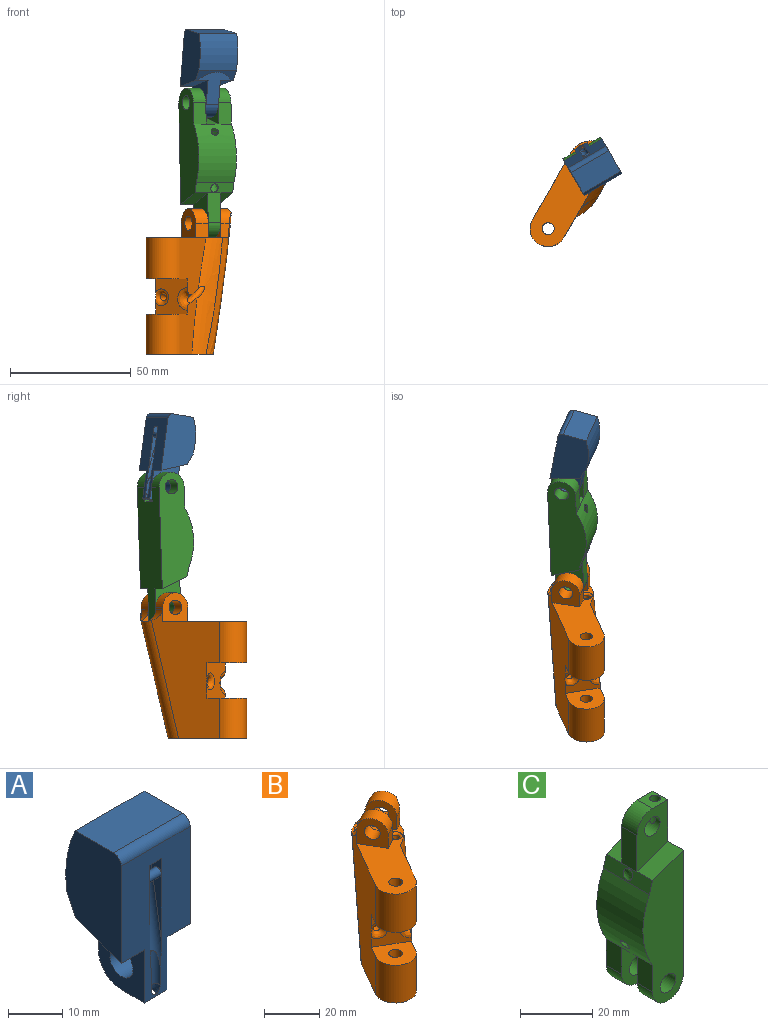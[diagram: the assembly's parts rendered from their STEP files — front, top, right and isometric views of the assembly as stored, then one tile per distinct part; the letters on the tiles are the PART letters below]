
ASSEMBLY  parts=3 mates=5
PART A: 30 faces, bbox 18x15.6x37.3 mm
  f0: cylinder r=5mm len=2.03mm, axis (-1,0,0), area 0.1mm2, adj f25,f29
  f1: plane 23.37x16mm, normal (0,1,0), area 258.7mm2, adj f4,f9,f10,f12,f13,f16,f17,f18
  f2: plane 18x4.63mm, normal (0,0.91,-0.42), area 48.6mm2, adj f7,f8,f12,f13,f15,f16
  f3: plane 6x5.9mm, normal (0,0,-1), area 28.7mm2, adj f4,f5,f9,f10,f28
  f4: cylinder r=6mm len=6mm, axis (-1,0,0), area 55.6mm2, adj f1,f3,f9,f10
  f5: plane 34x18mm, normal (0,-1,0), area 382.9mm2, adj f3,f7,f8,f9,f10,f12,f13,f14
  f6: plane 18x10mm, normal (0,0,1), area 180mm2, adj f7,f8,f14,f15
  f7: plane 24x14.5mm, normal (1,0,0), area 294.1mm2, adj f2,f5,f6,f12,f14,f15
  f8: plane 24x14.5mm, normal (-1,0,0), area 294.1mm2, adj f2,f5,f6,f13,f14,f15
  f9: plane 16.37x12mm, normal (1,0,0), area 134.2mm2, adj f1,f3,f4,f5,f11,f12
  f10: plane 16.37x12mm, normal (-1,0,0), area 134.2mm2, adj f1,f3,f4,f5,f11,f13
  f11: cylinder r=3mm len=6mm, axis (-1,0,0), area 111.2mm2, adj f9,f10
  f12: plane 12x6.05mm, normal (0,0.34,-0.94), area 77.3mm2, adj f1,f2,f5,f7,f9
  f13: plane 12x6.05mm, normal (0,0.34,-0.94), area 77.3mm2, adj f1,f2,f5,f8,f10
  f14: cylinder r=2mm len=18mm, axis (-1,0,0), area 56.5mm2, adj f5,f6,f7,f8
  f15: cylinder r=24.92mm len=18mm, axis (1,0,0), area 277.2mm2, adj f2,f6,f7,f8
  f16: cylinder r=19.67mm len=16mm, axis (0,0,-1), area 163.7mm2, adj f1,f2,f17,f18,f19,f20,f21
  f17: plane 16x1.7mm, normal (0,0,-1), area 18.3mm2, adj f1,f16
  f18: plane 3x1.7mm, normal (0,0,1), area 5mm2, adj f1,f16,f20,f21
  f19: plane 3x1.7mm, normal (0,0,-1), area 5mm2, adj f1,f16,f20,f21
  f20: plane 3.5x1.64mm, normal (-1,0,0), area 5.7mm2, adj f1,f16,f18,f19
  f21: plane 3.5x1.64mm, normal (1,0,0), area 5.7mm2, adj f1,f16,f18,f19
  f22: plane 4.48x3mm, normal (0,-0.16,-0.99), area 12.7mm2, adj f5,f23,f24,f25
  f23: plane 18.5x3mm, normal (-1,0,0), area 24.6mm2, adj f5,f22,f25,f26
  f24: plane 18.5x3mm, normal (1,0,0), area 24.6mm2, adj f5,f22,f25,f26
  f25: cylinder r=1.5mm len=23.99mm, axis (0,0.16,0.99), area 99mm2, adj f0,f5,f22,f23,f24,f27,f29
  f26: cylinder r=1mm len=3mm, axis (1,0,0), area 18.8mm2, adj f23,f24
  f27: cylinder r=5mm len=2.03mm, axis (-1,0,0), area 0.1mm2, adj f25,f29
  f28: bspline ~5.45x3.42mm, area 16.3mm2, adj f3,f5,f29
  f29: cylinder r=1.14mm len=7.64mm, axis (0,0,-1), area 24.2mm2, adj f0,f5,f25,f27,f28
PART B: 44 faces, bbox 55.1x59.7x84.5 mm
  f0: plane 23.52x12.49mm, normal (0.87,-0.5,0), area 223.6mm2, adj f5,f13,f24,f26,f28,f37,f38
  f1: plane 23.82x19mm, normal (0.87,-0.5,0), area 376.7mm2, adj f4,f14,f24,f25,f28,f37,f38
  f2: plane 46.47x11.49mm, normal (0.48,0.84,-0.26), area 93.2mm2, adj f13,f27,f29,f35
  f3: plane 55.07x30.05mm, normal (-0.87,0.5,0), area 1179mm2, adj f4,f5,f13,f14,f19,f24,f25,f26
  f4: cylinder r=7.5mm len=17mm, axis (0,0,-1), area 400.6mm2, adj f1,f3,f14,f25
  f5: cylinder r=7.5mm len=16.68mm, axis (0,0,-1), area 393.1mm2, adj f0,f3,f13,f26
  f6: cylinder r=2.5mm len=17mm, axis (0,0,-1), area 267mm2, adj f14,f25
  f7: plane 6x5.17mm, normal (0.5,-0.87,0), area 35.9mm2, adj f9,f14,f19,f21,f39
  f8: cylinder r=6mm len=13.38mm, axis (-0.87,-0.5,0), area 107.8mm2, adj f11,f15,f18,f20,f29
  f9: cylinder r=6mm len=13.38mm, axis (-0.87,-0.5,0), area 112.6mm2, adj f7,f17,f19,f21
  f10: cylinder r=3mm len=8.18mm, axis (-0.87,-0.5,0), area 112.6mm2, adj f18,f20
  f11: plane 5.23x3.05mm, normal (-0.5,0.87,0), area 6.1mm2, adj f8,f18,f20,f22,f33
  f12: plane 2.14x1.26mm, normal (0,0,1), area 0.1mm2, adj f18,f29
  f13: plane 33.94x29.32mm, normal (0,0,-1), area 511.2mm2, adj f0,f2,f3,f5,f23,f27,f28,f29
  f14: plane 55.62x46.23mm, normal (0,0,1), area 480.6mm2, adj f1,f3,f4,f6,f7,f15,f19,f20
  f15: plane 6.05x3.5mm, normal (0.5,-0.87,0), area 23.3mm2, adj f8,f14,f20,f29
  f16: cylinder r=3mm len=8.18mm, axis (-0.87,-0.5,0), area 112.6mm2, adj f19,f21
  f17: plane 5.17x2.99mm, normal (-0.5,0.87,0), area 6mm2, adj f9,f19,f21,f40
  f18: plane 12.11x8.98mm, normal (0.87,0.5,0), area 68.2mm2, adj f8,f10,f11,f12,f29,f30,f32,f33
  f19: plane 12x10.39mm, normal (-0.87,-0.5,0), area 100.3mm2, adj f3,f7,f9,f14,f16,f17
  f20: plane 13.28x12mm, normal (-0.87,-0.5,0), area 105.5mm2, adj f8,f10,f11,f14,f15,f22,f27
  f21: plane 13.27x12mm, normal (0.87,0.5,0), area 105.5mm2, adj f7,f9,f14,f16,f17,f27,f39,f40
  f22: cylinder r=5mm len=6.43mm, axis (0.87,0.5,0), area 21.6mm2, adj f11,f20,f27,f32,f33
  f23: cylinder r=2.5mm len=16.68mm, axis (0,0,-1), area 262.1mm2, adj f13,f26
  f24: plane 14.61x13mm, normal (-0.5,-0.87,0), area 150.5mm2, adj f0,f1,f3,f25,f26,f38,f43
  f25: plane 17x16.45mm, normal (0,0,-1), area 158.7mm2, adj f1,f3,f4,f6,f24
  f26: plane 17x16.45mm, normal (0,0,1), area 158.7mm2, adj f0,f3,f5,f23,f24
  f27: cylinder r=8.21mm len=53.82mm, axis (-0.13,-0.22,-0.97), area 639.3mm2, adj f2,f3,f13,f14,f20,f21,f22,f31
  f28: torus R=231.51mm, axis (-0.87,0.5,0), area 437.7mm2, adj f0,f1,f13,f14,f29,f37
  f29: bspline ~72.51x30.06mm, area 831.2mm2, adj f2,f8,f12,f13,f14,f15,f18,f28
  f30: cylinder r=2mm len=2.34mm, axis (0.5,-0.87,0), area 2.5mm2, adj f18,f32,f34
  f31: bspline ~23.14x9.91mm, area 7.2mm2, adj f27,f32,f34,f35,f36
  f32: bspline ~5.46x4.51mm, area 5.8mm2, adj f18,f22,f30,f31,f33,f34
  f33: bspline ~1.92x1.6mm, area 0.7mm2, adj f11,f18,f22,f32
  f34: bspline ~6.18x3.64mm, area 7.6mm2, adj f18,f29,f30,f31,f32,f35
  f35: bspline ~5.35x4.79mm, area 4.6mm2, adj f2,f31,f34,f36
  f36: bspline ~5.89x4.21mm, area 3.4mm2, adj f27,f31,f35
  f37: bspline ~26.33x19.54mm, area 272.8mm2, adj f0,f1,f28,f38,f39
  f38: bspline ~9.33x5.98mm, area 39.9mm2, adj f0,f1,f24,f37
  f39: bspline ~4.99x4.97mm, area 18.3mm2, adj f7,f14,f21,f37
  f40: cylinder r=5mm len=6.83mm, axis (0.87,0.5,0), area 24.2mm2, adj f3,f17,f21,f27
  f41: bspline ~25.69x24.89mm, area 375.9mm2, adj f42,f43
  f42: bspline ~5.96x5.94mm, area 30mm2, adj f14,f41
  f43: bspline ~7.01x6.08mm, area 43.8mm2, adj f3,f24,f41
PART C: 26 faces, bbox 17.2x18x62 mm
  f0: plane 9.05x5.95mm, normal (-1,0,0), area 53.8mm2, adj f6,f10,f14,f21
  f1: plane 9.05x5.95mm, normal (-1,0,0), area 53.8mm2, adj f7,f9,f13,f21
  f2: plane 12.37x5.9mm, normal (-1,0,0), area 73mm2, adj f5,f15,f16,f22
  f3: plane 56x18mm, normal (1,0,0), area 801.7mm2, adj f4,f6,f7,f9,f10,f12,f13,f14
  f4: plane 6x5.9mm, normal (0,0,1), area 28.3mm2, adj f3,f5,f15,f16,f25
  f5: cylinder r=6mm len=6mm, axis (0,1,0), area 55.6mm2, adj f2,f4,f15,f16
  f6: plane 48x15.76mm, normal (0,-1,0), area 574.8mm2, adj f0,f3,f10,f11,f19,f21,f22
  f7: plane 48x15.76mm, normal (0,1,0), area 574.8mm2, adj f1,f3,f8,f9,f18,f21,f22
  f8: cylinder r=3mm len=6mm, axis (0,1,0), area 112.2mm2, adj f7,f13
  f9: cylinder r=6mm len=12mm, axis (0,1,0), area 112.2mm2, adj f1,f3,f7,f13
  f10: cylinder r=6mm len=12mm, axis (0,1,0), area 112.2mm2, adj f0,f3,f6,f14
  f11: cylinder r=3mm len=6mm, axis (0,1,0), area 112.2mm2, adj f6,f14
  f12: plane 6.1x0.8mm, normal (0,0,-1), area 4.5mm2, adj f3,f13,f14,f20,f25
  f13: plane 15.05x12mm, normal (0,-1,0), area 117.7mm2, adj f1,f3,f8,f9,f12,f20
  f14: plane 15.05x12mm, normal (0,1,0), area 117.7mm2, adj f0,f3,f10,f11,f12,f20
  f15: plane 18.37x12mm, normal (0,1,0), area 158.2mm2, adj f2,f3,f4,f5,f17,f18
  f16: plane 18.37x12mm, normal (0,-1,0), area 158.2mm2, adj f2,f3,f4,f5,f17,f19
  f17: cylinder r=3mm len=6mm, axis (0,1,0), area 104.9mm2, adj f15,f16,f25
  f18: plane 12x6.05mm, normal (-0.34,0,0.94), area 77.3mm2, adj f3,f7,f15,f22
  f19: plane 12x6.05mm, normal (-0.34,0,0.94), area 77.3mm2, adj f3,f6,f16,f22
  f20: plane 11.2x6.1mm, normal (-0.26,0,-0.97), area 63.8mm2, adj f12,f13,f14,f21,f25
  f21: cylinder r=25.4mm len=24.42mm, axis (0,1,0), area 450.8mm2, adj f0,f1,f6,f7,f20,f22,f23,f24
  f22: plane 18x4.16mm, normal (-0.96,0,0.27), area 68.3mm2, adj f2,f6,f7,f18,f19,f21,f23
  f23: bspline ~26.8x13.05mm, area 242.7mm2, adj f21,f22,f24
  f24: bspline ~3.5x2.93mm, area 5.8mm2, adj f21,f23
  f25: cylinder r=1.5mm len=49.95mm, axis (0,0,-1), area 461mm2, adj f4,f12,f17,f20
PLACE A rot(axis=(-0.02,0.08,-1),150.1deg) t=(-12.51,43.18,88.61)mm
PLACE B t=(-89.36,4.27,-13.8)mm fixed
PLACE C rot(axis=(0.5,0.87,-0.01),178.2deg) t=(-13.29,44.33,48.8)mm
MATE planar A.f10 <-> C.f13  axis (0.87,0.5,0) through (-7.74,40.83,77.99)mm
MATE cylindrical C.f5 <-> B.f8  axis (0.87,0.5,0) through (-12.83,43.54,23.82)mm
MATE planar A.f10 <-> C.f13  axis (0.87,0.5,0) through (-7.74,40.83,77.99)mm
MATE planar C.f16 <-> B.f21  axis (-0.87,-0.5,0) through (-15.39,42.06,26.67)mm
MATE cylindrical C.f8 <-> A.f4  axis (0.87,0.5,0) through (-18.96,42.11,73.78)mm
